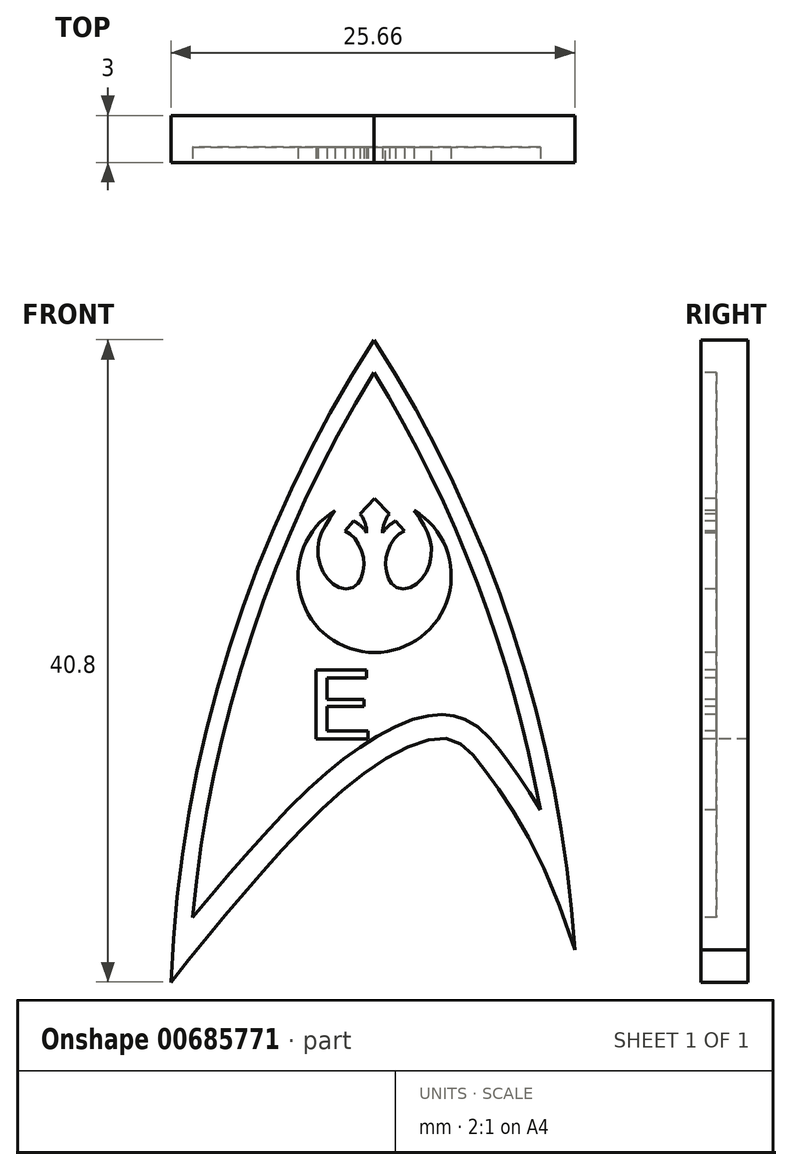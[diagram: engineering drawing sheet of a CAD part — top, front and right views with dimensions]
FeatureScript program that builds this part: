
annotation { "Feature Type Name" : "Feature", "Feature Type Description" : "" }
export const myFeature = defineFeature(function(context is Context, id is Id, definition is map)
    precondition{}
    {
        {
            var Q0;
            Q0=qCreatedBy(makeId("Front.planeOp"),FACE);
            var sketch = newSketch(context, id + "F0", { "sketchPlane" : qUnion([Q0])});
            skArc(sketch, "E0", {"start": v(19.2, -4.61) * mm, "mid": v(10.02, -24.15) * mm, "end": v(6.3, -45.41) * mm});
            skArc(sketch, "E1", {"start": v(31.96, -43.38) * mm, "mid": v(28.04, -23.19) * mm, "end": v(19.2, -4.61) * mm});
            skFitSpline(sketch, "E2", {"points": [v(6.3, -45.41) * mm, v(12.28, -38.24) * mm, v(18.74, -32.04) * mm, v(23.82, -29.95) * mm, v(26.3, -32.01) * mm, v(31.96, -43.38) * mm], "startDerivative": vector(25.76, 32.65) * mm, "endDerivative": vector(21.78, -69.9) * mm});
            skSolve(sketch);
        }
        {
            var Q0;
            Q0=qSketchRegion(id+"F0",true);
            extrude(context, id + "F1", {"entities" : qUnion([Q0]), "depth" : 3 * mm, "offsetDistance" : 25 * mm});
        }
        {
            var Q0;
            Q0=makeQuery(id+"F1.opExtrude","CAP_FACE",FACE,{"disambiguationData":[OSD([sQuery(id+"F0.wireOp",EDGE,"E0"),sQuery(id+"F0.wireOp",EDGE,"E1"),sQuery(id+"F0.wireOp",EDGE,"E2")])],"isStart":false});
            var sketch = newSketch(context, id + "F2", { "sketchPlane" : qUnion([Q0])});
            skArc(sketch, "E3.0", {"start": v(19.2, -6.68) * mm, "mid": v(11.44, -23.34) * mm, "end": v(7.67, -41.32) * mm});
            skArc(sketch, "E3.1", {"start": v(29.77, -34.51) * mm, "mid": v(25.78, -20.1) * mm, "end": v(19.2, -6.68) * mm});
            skFitSpline(sketch, "E4.0", {"points": [v(5.12, -44.48) * mm, v(5.66, -43.8) * mm, v(6.76, -42.43) * mm, v(8.44, -40.38) * mm, v(10.17, -38.36) * mm, v(11.93, -36.35) * mm, v(13.77, -34.38) * mm, v(15.38, -32.83) * mm, v(16.72, -31.68) * mm, v(17.77, -30.87) * mm, v(18.86, -30.12) * mm, v(19.97, -29.47) * mm, v(21.09, -28.94) * mm, v(22.03, -28.62) * mm, v(22.8, -28.47) * mm, v(23.39, -28.41) * mm, v(23.9, -28.44) * mm, v(24.3, -28.51) * mm, v(24.7, -28.62) * mm, v(25.16, -28.8) * mm, v(25.81, -29.2) * mm, v(26.46, -29.8) * mm, v(26.98, -30.43) * mm, v(27.38, -30.96) * mm, v(27.77, -31.48) * mm, v(28.3, -32.22) * mm, v(28.99, -33.23) * mm, v(29.7, -34.39) * mm, v(30.7, -36.14) * mm, v(31.95, -38.77) * mm, v(32.92, -41.43) * mm, v(33.4, -42.93) * mm]});
            skEllipse(sketch, "E5", {"center": v(12.77, -27.77) * mm, "majorRadius": 1.73 * mm, "minorRadius": 1.4 * mm, "majorAxis": v(0, 1)});
            skLineSegment(sketch, "E6", {"start": v(11.37, -27.77) * mm, "end": v(14.16, -27.77) * mm, "construction": true});
            skLineSegment(sketch, "E7", {"start": v(15.52, -25.6) * mm, "end": v(15.52, -29.96) * mm});
            skLineSegment(sketch, "E8", {"start": v(15.52, -29.96) * mm, "end": v(18.8, -29.96) * mm});
            skLineSegment(sketch, "E9", {"start": v(18.8, -29.96) * mm, "end": v(18.8, -29.46) * mm});
            skLineSegment(sketch, "E10", {"start": v(18.8, -29.46) * mm, "end": v(16.2, -29.46) * mm});
            skLineSegment(sketch, "E11", {"start": v(16.2, -29.46) * mm, "end": v(16.2, -27.91) * mm});
            skLineSegment(sketch, "E12", {"start": v(16.2, -27.91) * mm, "end": v(18.56, -27.91) * mm});
            skLineSegment(sketch, "E13", {"start": v(18.56, -27.91) * mm, "end": v(18.56, -27.45) * mm});
            skLineSegment(sketch, "E14", {"start": v(18.56, -27.45) * mm, "end": v(16.2, -27.45) * mm});
            skLineSegment(sketch, "E15", {"start": v(16.2, -27.45) * mm, "end": v(16.2, -26.1) * mm});
            skLineSegment(sketch, "E16", {"start": v(16.2, -26.1) * mm, "end": v(18.71, -26.1) * mm});
            skLineSegment(sketch, "E17", {"start": v(18.71, -26.1) * mm, "end": v(18.71, -25.6) * mm});
            skLineSegment(sketch, "E18", {"start": v(18.71, -25.6) * mm, "end": v(15.52, -25.6) * mm});
            skLineSegment(sketch, "E19", {"start": v(15.52, -25.6) * mm, "end": v(11.4, -25.6) * mm, "construction": true});
            skLineSegment(sketch, "E20", {"start": v(15.52, -29.96) * mm, "end": v(11.36, -29.96) * mm, "construction": true});
            skFitSpline(sketch, "E21.0", {"points": [v(13.66, -25.47) * mm, v(12.77, -25.25) * mm, v(11.87, -25.47) * mm, v(11.18, -26.06) * mm, v(10.76, -26.86) * mm, v(10.62, -27.77) * mm, v(10.76, -28.67) * mm, v(11.18, -29.48) * mm, v(11.87, -30.06) * mm, v(12.77, -30.29) * mm, v(13.66, -30.06) * mm, v(14.35, -29.48) * mm, v(14.77, -28.67) * mm, v(14.92, -27.77) * mm, v(14.77, -26.86) * mm, v(14.35, -26.06) * mm, v(13.66, -25.47) * mm, v(12.77, -25.25) * mm, v(11.87, -25.47) * mm]});
            skArc(sketch, "E22", {"start": v(14.44, -26.3) * mm, "mid": v(12.73, -25.47) * mm, "end": v(11.05, -26.36) * mm});
            skArc(sketch, "E23.MirrorCS", {"start": v(14.44, -29.23) * mm, "mid": v(12.73, -30.06) * mm, "end": v(11.05, -29.18) * mm});
            skFitSpline(sketch, "E24.trimOffspring", {"points": [v(13.65, -25.48) * mm, v(12.77, -25.26) * mm, v(11.88, -25.48) * mm, v(11.2, -26.07) * mm, v(10.77, -26.87) * mm, v(10.63, -27.77) * mm, v(10.77, -28.67) * mm, v(11.2, -29.47) * mm, v(11.88, -30.05) * mm, v(12.77, -30.28) * mm, v(13.65, -30.05) * mm, v(14.34, -29.47) * mm, v(14.76, -28.67) * mm, v(14.9, -27.77) * mm, v(14.76, -26.87) * mm, v(14.34, -26.07) * mm, v(13.65, -25.48) * mm, v(12.77, -25.26) * mm, v(11.88, -25.48) * mm]});
            skPoint(sketch, "E25.orphan", {"position": v(17.34, -25.74) * mm});
            skArc(sketch, "E26", {"start": v(16.75, -15.44) * mm, "mid": v(19.23, -24.48) * mm, "end": v(21.76, -15.45) * mm});
            skFitSpline(sketch, "E27", {"points": [v(21.76, -15.45) * mm, v(22.5, -16.64) * mm, v(22.84, -17.7) * mm, v(22.7, -18.94) * mm, v(22.12, -19.9) * mm, v(21.28, -20.41) * mm, v(20.47, -20.25) * mm, v(20.1, -19.7) * mm, v(19.93, -18.78) * mm, v(20.1, -17.94) * mm, v(20.57, -17.16) * mm, v(21.13, -16.75) * mm], "startDerivative": vector(7.46, -10.98) * mm, "endDerivative": vector(7.61, 4.47) * mm});
            skLineSegment(sketch, "E28", {"start": v(21.13, -16.75) * mm, "end": v(20.58, -16.13) * mm});
            skArc(sketch, "E29", {"start": v(20.58, -16.13) * mm, "mid": v(20.11, -16.45) * mm, "end": v(19.75, -16.88) * mm});
            skArc(sketch, "E30", {"start": v(20.17, -15.67) * mm, "mid": v(19.86, -16.24) * mm, "end": v(19.75, -16.88) * mm});
            skLineSegment(sketch, "E31", {"start": v(19.24, -19.61) * mm, "end": v(19.24, -13.75) * mm});
            skFitSpline(sketch, "E32.MirrorCS", {"points": [v(16.73, -15.45) * mm, v(15.99, -16.64) * mm, v(15.65, -17.7) * mm, v(15.78, -18.94) * mm, v(16.36, -19.9) * mm, v(17.2, -20.41) * mm, v(18.02, -20.25) * mm, v(18.4, -19.7) * mm, v(18.56, -18.78) * mm, v(18.38, -17.94) * mm, v(17.92, -17.16) * mm, v(17.36, -16.75) * mm], "startDerivative": vector(-7.46, -10.98) * mm, "endDerivative": vector(-7.61, 4.47) * mm});
            skLineSegment(sketch, "E33.MirrorCS", {"start": v(17.36, -16.75) * mm, "end": v(17.9, -16.13) * mm});
            skArc(sketch, "E34.MirrorCS", {"start": v(17.9, -16.13) * mm, "mid": v(18.37, -16.45) * mm, "end": v(18.74, -16.88) * mm});
            skArc(sketch, "E35.MirrorCS", {"start": v(18.32, -15.67) * mm, "mid": v(18.63, -16.24) * mm, "end": v(18.74, -16.88) * mm});
            skPoint(sketch, "E36", {"position": v(19.24, -14.6) * mm});
            skLineSegment(sketch, "E37", {"start": v(18.32, -15.67) * mm, "end": v(19.24, -14.68) * mm});
            skLineSegment(sketch, "E38", {"start": v(19.24, -14.68) * mm, "end": v(20.17, -15.67) * mm});
            skSolve(sketch);
        }
        {
            var Q0;
            Q0=makeQuery(id+"F2.imprint","IMPRINT",FACE,{"disambiguationData":[TD([[makeQuery(id+"F2.imprint","IMPRINT",EDGE,{"derivedFrom":sQuery(id+"F2.wireOp",EDGE,"E3.0")}),1.0]])]});
            var Q1;
            Q1=makeQuery(id+"F2.imprint","IMPRINT",FACE,{"disambiguationData":[TD([[makeQuery(id+"F2.imprint","IMPRINT",EDGE,{"derivedFrom":sQuery(id+"F2.wireOp",EDGE,"E5")}),1.0]])]});
            extrude(context, id + "F3", {"entities" : qUnion([Q0, Q1]), "operationType" : NewBodyOperationType.REMOVE, "oppositeDirection" : true, "depth" : 1 * mm, "offsetDistance" : 25 * mm});
        }
    });
